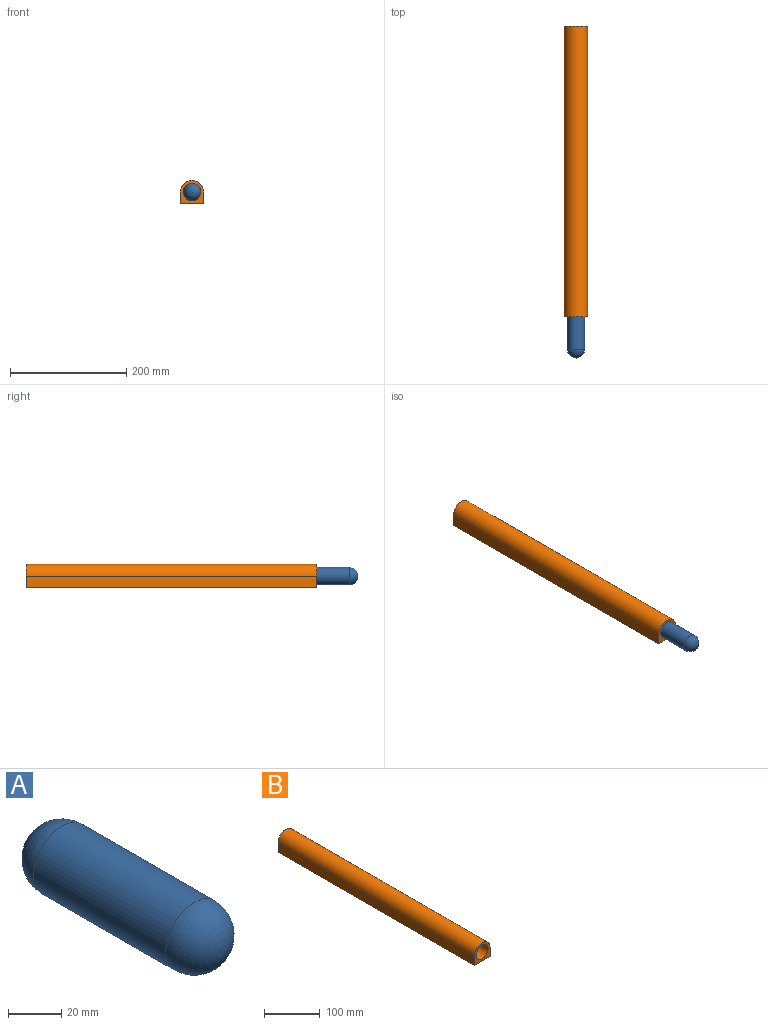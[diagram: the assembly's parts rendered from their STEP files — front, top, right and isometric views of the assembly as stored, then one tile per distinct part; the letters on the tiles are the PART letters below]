
ASSEMBLY  parts=2 mates=1
PART A: 3 faces, bbox 30x100x30 mm
  f0: cylinder r=15mm len=70mm, axis (0,-1,0), area 6597.3mm2, adj f1,f2
  f1: sphere r=15mm, area 1413.7mm2, adj f0
  f2: sphere r=15mm, area 1413.7mm2, adj f0
PART B: 7 faces, bbox 40x500x40 mm
  f0: plane 500x20mm, normal (-1,0,0), area 10000mm2, adj f1,f4,f5,f6
  f1: plane 500x40mm, normal (0,0,-1), area 20000mm2, adj f0,f2,f4,f5
  f2: plane 500x20mm, normal (1,0,0), area 10000mm2, adj f1,f4,f5,f6
  f3: cylinder r=15mm len=500mm, axis (0,-1,0), area 47123.9mm2, adj f4,f5
  f4: plane 40x40mm, normal (0,1,0), area 721.5mm2, adj f0,f1,f2,f3,f6
  f5: plane 40x40mm, normal (0,-1,0), area 721.5mm2, adj f0,f1,f2,f3,f6
  f6: cylinder r=20mm len=500mm, axis (0,-1,0), area 31415.9mm2, adj f0,f2,f4,f5
PLACE A t=(-20,-71.03,20)mm
PLACE B t=(-20,0,0)mm
MATE slider A.f0 <-> B.f3  axis (0,-1,0) through (-20,-21.03,20)mm
